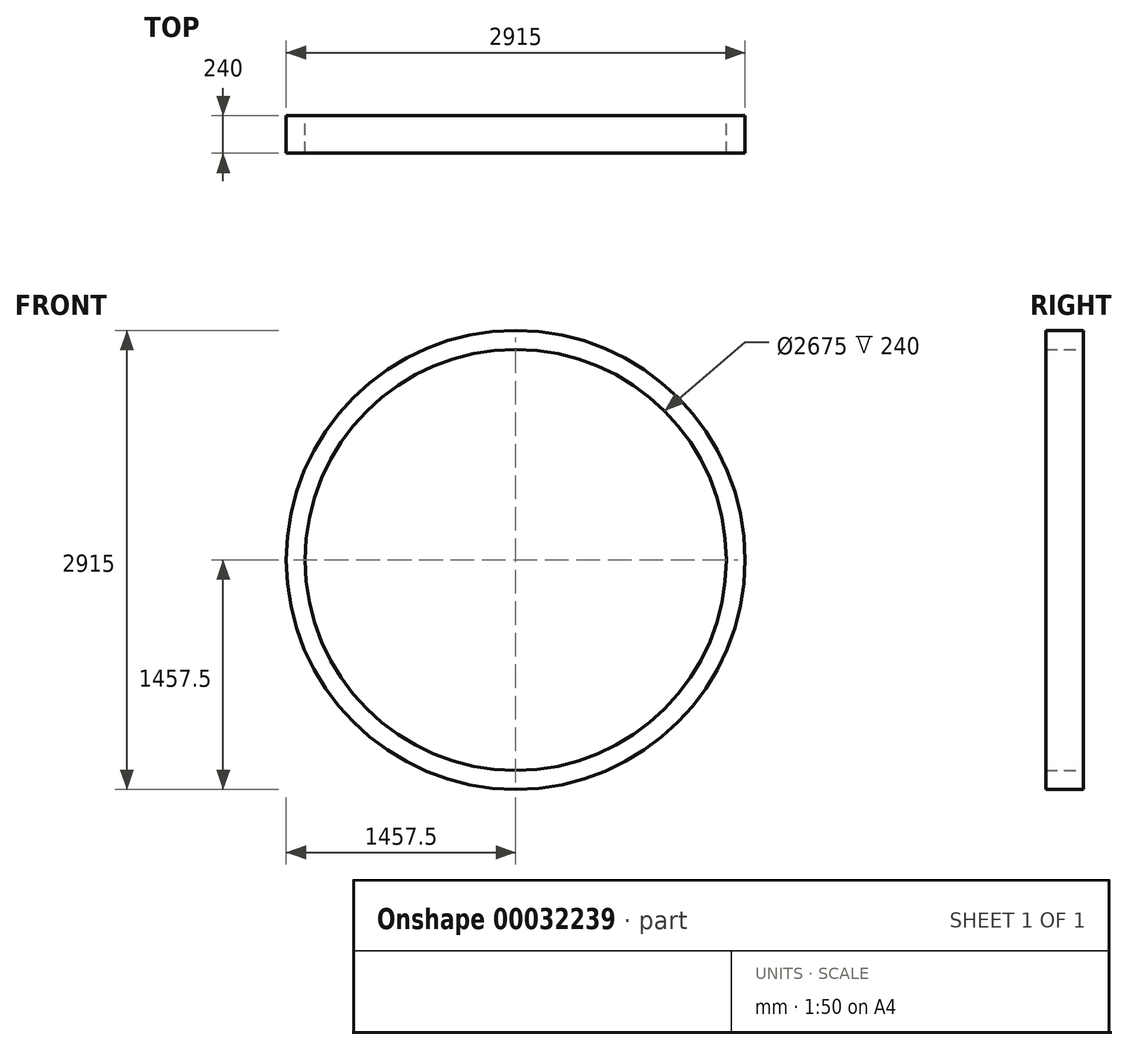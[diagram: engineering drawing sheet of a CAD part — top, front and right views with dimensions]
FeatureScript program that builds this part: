
annotation { "Feature Type Name" : "Feature", "Feature Type Description" : "" }
export const myFeature = defineFeature(function(context is Context, id is Id, definition is map)
    precondition{}
    {
        {
            var Q0;
            Q0=qCreatedBy(makeId("Front.planeOp"),FACE);
            var sketch = newSketch(context, id + "F0", { "sketchPlane" : qUnion([Q0])});
            skCircle(sketch, "E0", {"center": v(0, 0) * mm, "radius": 1457.5 * mm});
            skCircle(sketch, "E1", {"center": v(0, 0) * mm, "radius": 1337.5 * mm});
            skSolve(sketch);
        }
        {
            var Q0;
            Q0=makeQuery(id+"F0.imprint","IMPRINT",FACE,{"disambiguationData":[TD([[makeQuery(id+"F0.imprint","IMPRINT",EDGE,{"derivedFrom":sQuery(id+"F0.wireOp",EDGE,"E0")}),1.0]])]});
            extrude(context, id + "F1", {"entities" : qUnion([Q0]), "depth" : 240 * mm});
        }
    });
